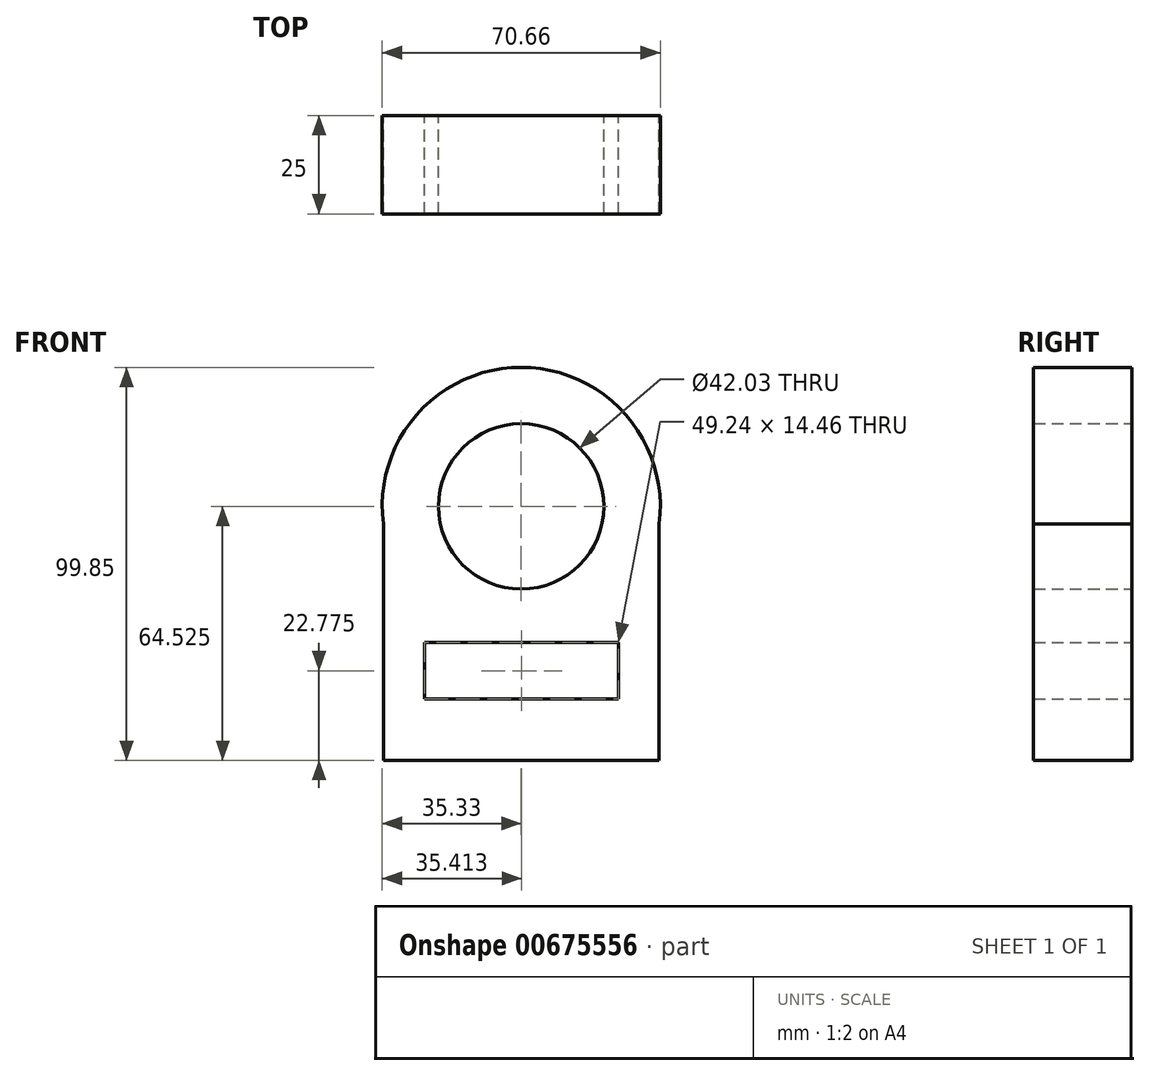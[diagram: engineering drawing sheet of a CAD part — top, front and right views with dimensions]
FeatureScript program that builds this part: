
annotation { "Feature Type Name" : "Feature", "Feature Type Description" : "" }
export const myFeature = defineFeature(function(context is Context, id is Id, definition is map)
    precondition{}
    {
        {
            var Q0;
            Q0=qCreatedBy(makeId("Front.planeOp"),FACE);
            var sketch = newSketch(context, id + "F0", { "sketchPlane" : qUnion([Q0])});
            skLineSegment(sketch, "E0", {"start": v(0, 0) * mm, "end": v(0, -60) * mm});
            skLineSegment(sketch, "E1", {"start": v(0, -60) * mm, "end": v(70.08, -60) * mm});
            skLineSegment(sketch, "E2", {"start": v(70.08, -60) * mm, "end": v(70.08, 0) * mm});
            skArc(sketch, "E3", {"start": v(70.08, 0) * mm, "mid": v(35.04, 39.84) * mm, "end": v(0, 0) * mm});
            skCircle(sketch, "E4", {"center": v(35.04, 4.51) * mm, "radius": 21.01 * mm});
            skLineSegment(sketch, "E5", {"start": v(10.5, -30) * mm, "end": v(10.5, -44.47) * mm});
            skLineSegment(sketch, "E6", {"start": v(59.74, -44.47) * mm, "end": v(59.74, -30) * mm});
            skLineSegment(sketch, "E7", {"start": v(10.5, -30) * mm, "end": v(59.74, -30) * mm});
            skLineSegment(sketch, "E8", {"start": v(10.5, -44.47) * mm, "end": v(59.74, -44.47) * mm});
            skSolve(sketch);
        }
        {
            var Q0;
            Q0 = qSketchRegion(id + "F0", true);
            extrude(context, id + "F1", {"entities" : qUnion([Q0]), "depth" : 25 * mm, "offsetDistance" : 25 * mm});
        }
    });
